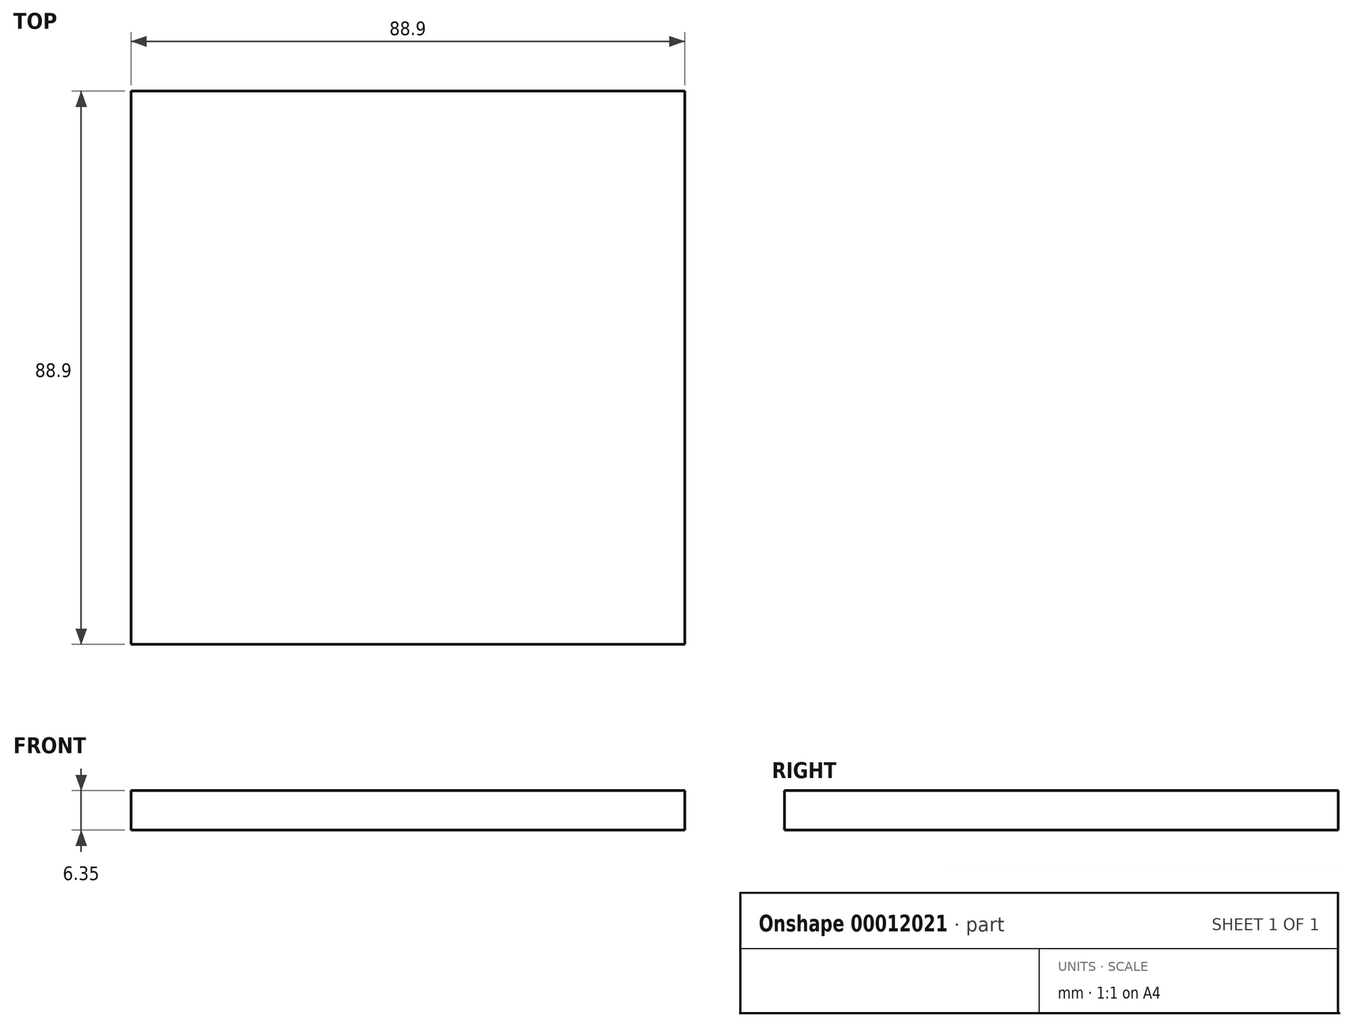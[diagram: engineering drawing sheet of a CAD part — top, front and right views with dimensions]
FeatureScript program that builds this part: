
annotation { "Feature Type Name" : "Feature", "Feature Type Description" : "" }
export const myFeature = defineFeature(function(context is Context, id is Id, definition is map)
    precondition{}
    {
        {
            var Q0;
            Q0=qCreatedBy(makeId("Top.planeOp"),FACE);
            var sketch = newSketch(context, id + "F0", { "sketchPlane" : qUnion([Q0])});
            skLineSegment(sketch, "E0.bottom", {"start": v(114.47, 9.04) * mm, "end": v(25.57, 9.04) * mm});
            skLineSegment(sketch, "E0.top", {"start": v(114.47, 97.94) * mm, "end": v(25.57, 97.94) * mm});
            skLineSegment(sketch, "E0.left", {"start": v(114.47, 9.04) * mm, "end": v(114.47, 97.94) * mm});
            skLineSegment(sketch, "E0.right", {"start": v(25.57, 9.04) * mm, "end": v(25.57, 97.94) * mm});
            skSolve(sketch);
        }
        {
            var Q0;
            Q0=makeQuery(id+"F0.imprint","IMPRINT",FACE,{"disambiguationData":[TD([[makeQuery(id+"F0.imprint","IMPRINT",EDGE,{"derivedFrom":sQuery(id+"F0.wireOp",EDGE,"E0.bottom")}),-1.0]])]});
            extrude(context, id + "F1", {"entities" : qUnion([Q0]), "depth" : 6.35 * mm});
        }
    });
